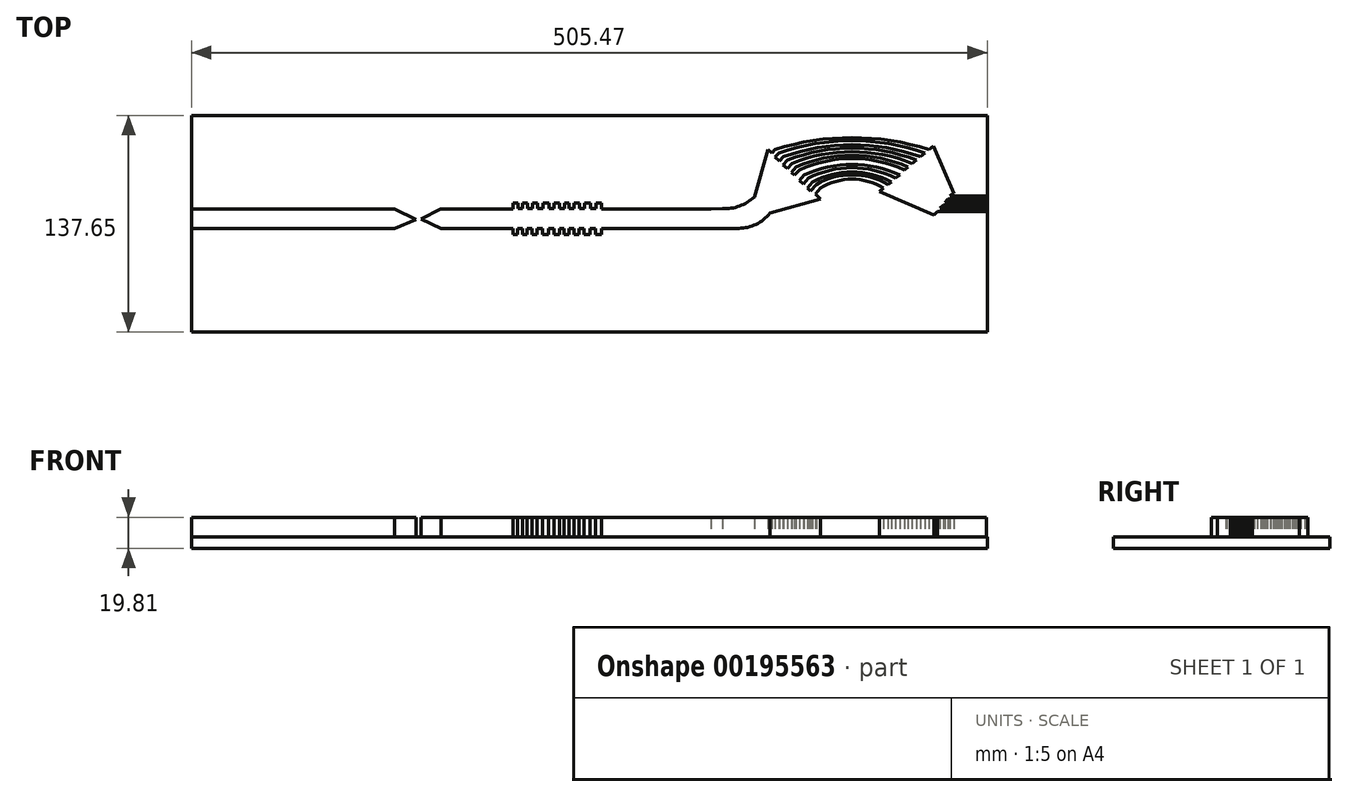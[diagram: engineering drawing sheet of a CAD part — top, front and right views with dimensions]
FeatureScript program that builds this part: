
annotation { "Feature Type Name" : "Feature", "Feature Type Description" : "" }
export const myFeature = defineFeature(function(context is Context, id is Id, definition is map)
    precondition{}
    {
        {
            var Q0;
            Q0=qCreatedBy(makeId("Top.planeOp"),FACE);
            var sketch = newSketch(context, id + "F0", { "sketchPlane" : qUnion([Q0])});
            skLineSegment(sketch, "E0.bottom", {"start": v(-20.52, -68.03) * mm, "end": v(484.95, -68.03) * mm});
            skLineSegment(sketch, "E0.top", {"start": v(-20.52, 69.62) * mm, "end": v(484.95, 69.62) * mm});
            skLineSegment(sketch, "E0.left", {"start": v(-20.52, -68.03) * mm, "end": v(-20.52, 69.62) * mm});
            skLineSegment(sketch, "E0.right", {"start": v(484.95, -68.03) * mm, "end": v(484.95, 69.62) * mm});
            skSolve(sketch);
        }
        {
            var Q0;
            Q0=qSketchRegion(id+"F0",true);
            extrude(context, id + "F1", {"entities" : qUnion([Q0]), "depth" : 7.37 * mm});
        }
        {
            var Q0;
            Q0=makeQuery(id+"F1.opExtrude","CAP_FACE",FACE,{"disambiguationData":[OSD([sQuery(id+"F0.wireOp",EDGE,"E0.bottom"),sQuery(id+"F0.wireOp",EDGE,"E0.top"),sQuery(id+"F0.wireOp",EDGE,"E0.left"),sQuery(id+"F0.wireOp",EDGE,"E0.right")])],"isStart":false});
            var sketch = newSketch(context, id + "F2", { "sketchPlane" : qUnion([Q0])});
            skLineSegment(sketch, "E1", {"start": v(183.86, 10.27) * mm, "end": v(183.86, 14.18) * mm});
            skLineSegment(sketch, "E2", {"start": v(183.86, 14.18) * mm, "end": v(186.92, 14.18) * mm});
            skLineSegment(sketch, "E3", {"start": v(186.92, 14.18) * mm, "end": v(186.92, 10.42) * mm});
            skLineSegment(sketch, "E4", {"start": v(186.92, 10.42) * mm, "end": v(189.9, 10.42) * mm});
            skLineSegment(sketch, "E5", {"start": v(189.9, 10.42) * mm, "end": v(189.9, 14.18) * mm});
            skLineSegment(sketch, "E6", {"start": v(189.9, 14.18) * mm, "end": v(192.9, 14.18) * mm});
            skLineSegment(sketch, "E7", {"start": v(192.9, 14.18) * mm, "end": v(192.9, 10.42) * mm});
            skLineSegment(sketch, "E8", {"start": v(192.9, 10.42) * mm, "end": v(196.13, 10.42) * mm});
            skLineSegment(sketch, "E9", {"start": v(196.13, 10.42) * mm, "end": v(196.13, 14.18) * mm});
            skLineSegment(sketch, "E10", {"start": v(196.13, 14.18) * mm, "end": v(199.35, 14.18) * mm});
            skLineSegment(sketch, "E11", {"start": v(199.35, 14.18) * mm, "end": v(199.35, 10.42) * mm});
            skLineSegment(sketch, "E12", {"start": v(199.35, 10.42) * mm, "end": v(202.73, 10.42) * mm});
            skLineSegment(sketch, "E13", {"start": v(202.73, 10.42) * mm, "end": v(202.73, 14.18) * mm});
            skLineSegment(sketch, "E14", {"start": v(202.73, 14.18) * mm, "end": v(206.5, 14.18) * mm});
            skLineSegment(sketch, "E15", {"start": v(206.5, 14.18) * mm, "end": v(206.5, 10.42) * mm});
            skLineSegment(sketch, "E16", {"start": v(206.5, 10.42) * mm, "end": v(209.87, 10.42) * mm});
            skLineSegment(sketch, "E17", {"start": v(209.87, 10.42) * mm, "end": v(209.87, 14.18) * mm});
            skLineSegment(sketch, "E18", {"start": v(209.87, 14.18) * mm, "end": v(213.4, 14.18) * mm});
            skLineSegment(sketch, "E19", {"start": v(213.4, 14.18) * mm, "end": v(213.4, 10.42) * mm});
            skLineSegment(sketch, "E20.MirrorCS", {"start": v(186.66, -5.84) * mm, "end": v(186.66, -2.08) * mm});
            skLineSegment(sketch, "E21.MirrorCS", {"start": v(199.1, -2.08) * mm, "end": v(202.48, -2.08) * mm});
            skLineSegment(sketch, "E22.MirrorCS", {"start": v(199.1, -5.84) * mm, "end": v(199.1, -2.08) * mm});
            skLineSegment(sketch, "E23.MirrorCS", {"start": v(189.66, -2.08) * mm, "end": v(189.66, -5.84) * mm});
            skLineSegment(sketch, "E24.MirrorCS", {"start": v(186.66, -2.08) * mm, "end": v(189.66, -2.08) * mm});
            skLineSegment(sketch, "E25.MirrorCS", {"start": v(202.48, -2.08) * mm, "end": v(202.48, -5.84) * mm});
            skLineSegment(sketch, "E26.MirrorCS", {"start": v(189.66, -5.84) * mm, "end": v(192.65, -5.84) * mm});
            skLineSegment(sketch, "E27.MirrorCS", {"start": v(202.48, -5.84) * mm, "end": v(206.24, -5.84) * mm});
            skLineSegment(sketch, "E28.MirrorCS", {"start": v(192.65, -5.84) * mm, "end": v(192.65, -2.08) * mm});
            skLineSegment(sketch, "E29.MirrorCS", {"start": v(192.65, -2.08) * mm, "end": v(195.87, -2.08) * mm});
            skLineSegment(sketch, "E30.MirrorCS", {"start": v(206.24, -5.84) * mm, "end": v(206.24, -2.08) * mm});
            skLineSegment(sketch, "E31.MirrorCS", {"start": v(195.87, -2.08) * mm, "end": v(195.87, -5.84) * mm});
            skLineSegment(sketch, "E32.MirrorCS", {"start": v(183.6, -5.84) * mm, "end": v(186.66, -5.84) * mm});
            skLineSegment(sketch, "E33.MirrorCS", {"start": v(206.24, -2.08) * mm, "end": v(209.62, -2.08) * mm});
            skLineSegment(sketch, "E34.MirrorCS", {"start": v(209.62, -2.08) * mm, "end": v(209.62, -5.84) * mm});
            skLineSegment(sketch, "E35.MirrorCS", {"start": v(195.87, -5.84) * mm, "end": v(199.1, -5.84) * mm});
            skLineSegment(sketch, "E36.MirrorCS", {"start": v(209.62, -5.84) * mm, "end": v(213.15, -5.84) * mm});
            skLineSegment(sketch, "E37.MirrorCS", {"start": v(183.61, -2.15) * mm, "end": v(183.6, -5.84) * mm});
            skLineSegment(sketch, "E38.MirrorCS", {"start": v(213.15, -5.84) * mm, "end": v(213.15, -2.08) * mm});
            skLineSegment(sketch, "E39", {"start": v(213.4, 10.42) * mm, "end": v(216.4, 10.42) * mm});
            skLineSegment(sketch, "E40", {"start": v(216.4, 10.42) * mm, "end": v(216.4, 14.18) * mm});
            skLineSegment(sketch, "E41", {"start": v(216.4, 14.18) * mm, "end": v(219.39, 14.18) * mm});
            skLineSegment(sketch, "E42", {"start": v(219.39, 14.18) * mm, "end": v(219.39, 10.42) * mm});
            skLineSegment(sketch, "E43", {"start": v(219.39, 10.42) * mm, "end": v(222.61, 10.42) * mm});
            skLineSegment(sketch, "E44", {"start": v(222.61, 10.42) * mm, "end": v(222.61, 14.18) * mm});
            skLineSegment(sketch, "E45", {"start": v(222.61, 14.18) * mm, "end": v(225.84, 14.18) * mm});
            skLineSegment(sketch, "E46", {"start": v(225.84, 14.18) * mm, "end": v(225.84, 10.42) * mm});
            skLineSegment(sketch, "E47", {"start": v(225.84, 10.42) * mm, "end": v(229.22, 10.42) * mm});
            skLineSegment(sketch, "E48", {"start": v(229.22, 10.42) * mm, "end": v(229.22, 14.18) * mm});
            skLineSegment(sketch, "E49", {"start": v(229.22, 14.18) * mm, "end": v(232.98, 14.18) * mm});
            skLineSegment(sketch, "E50", {"start": v(232.98, 14.18) * mm, "end": v(232.98, 10.42) * mm});
            skLineSegment(sketch, "E51", {"start": v(232.98, 10.42) * mm, "end": v(236.36, 10.42) * mm});
            skLineSegment(sketch, "E52", {"start": v(236.36, 10.42) * mm, "end": v(236.36, 14.18) * mm});
            skLineSegment(sketch, "E53", {"start": v(236.36, 14.18) * mm, "end": v(239.89, 14.18) * mm});
            skLineSegment(sketch, "E54", {"start": v(239.89, 14.18) * mm, "end": v(239.89, 10.33) * mm});
            skLineSegment(sketch, "E55.MirrorCS", {"start": v(225.58, -2.08) * mm, "end": v(228.96, -2.08) * mm});
            skLineSegment(sketch, "E56.MirrorCS", {"start": v(225.58, -5.84) * mm, "end": v(225.58, -2.08) * mm});
            skLineSegment(sketch, "E57.MirrorCS", {"start": v(216.14, -2.08) * mm, "end": v(216.14, -5.84) * mm});
            skLineSegment(sketch, "E58.MirrorCS", {"start": v(213.15, -2.08) * mm, "end": v(216.14, -2.08) * mm});
            skLineSegment(sketch, "E59.MirrorCS", {"start": v(228.96, -2.08) * mm, "end": v(228.96, -5.84) * mm});
            skLineSegment(sketch, "E60.MirrorCS", {"start": v(216.14, -5.84) * mm, "end": v(219.14, -5.84) * mm});
            skLineSegment(sketch, "E61.MirrorCS", {"start": v(228.96, -5.84) * mm, "end": v(232.72, -5.84) * mm});
            skLineSegment(sketch, "E62.MirrorCS", {"start": v(219.14, -5.84) * mm, "end": v(219.14, -2.08) * mm});
            skLineSegment(sketch, "E63.MirrorCS", {"start": v(219.14, -2.08) * mm, "end": v(222.36, -2.08) * mm});
            skLineSegment(sketch, "E64.MirrorCS", {"start": v(232.72, -5.84) * mm, "end": v(232.72, -2.08) * mm});
            skLineSegment(sketch, "E65.MirrorCS", {"start": v(222.36, -2.08) * mm, "end": v(222.36, -5.84) * mm});
            skLineSegment(sketch, "E66.MirrorCS", {"start": v(232.72, -2.08) * mm, "end": v(236.1, -2.08) * mm});
            skLineSegment(sketch, "E67.MirrorCS", {"start": v(236.1, -2.08) * mm, "end": v(236.1, -5.84) * mm});
            skLineSegment(sketch, "E68.MirrorCS", {"start": v(222.36, -5.84) * mm, "end": v(225.58, -5.84) * mm});
            skLineSegment(sketch, "E69.MirrorCS", {"start": v(236.1, -5.84) * mm, "end": v(239.89, -5.84) * mm});
            skLineSegment(sketch, "E70.MirrorCS", {"start": v(239.89, -5.84) * mm, "end": v(239.89, -2.04) * mm});
            skLineSegment(sketch, "E71", {"start": v(183.86, 10.27) * mm, "end": v(181.75, 10.28) * mm});
            skLineSegment(sketch, "E72", {"start": v(183.61, -2.15) * mm, "end": v(181.73, -2.15) * mm});
            skLineSegment(sketch, "E73", {"start": v(345.62, 48.01) * mm, "end": v(348.2, 45.76) * mm});
            skLineSegment(sketch, "E74", {"start": v(348.2, 45.76) * mm, "end": v(350.17, 48.01) * mm});
            skLineSegment(sketch, "E75", {"start": v(352.55, 45.93) * mm, "end": v(350.17, 43.2) * mm});
            skLineSegment(sketch, "E76", {"start": v(350.17, 43.2) * mm, "end": v(353.08, 40.66) * mm});
            skLineSegment(sketch, "E77", {"start": v(353.08, 40.66) * mm, "end": v(355.57, 43.5) * mm});
            skLineSegment(sketch, "E78", {"start": v(358.09, 41.3) * mm, "end": v(355.33, 38.15) * mm});
            skLineSegment(sketch, "E79", {"start": v(355.33, 38.15) * mm, "end": v(358.04, 35.78) * mm});
            skLineSegment(sketch, "E80", {"start": v(358.04, 35.78) * mm, "end": v(361.02, 39.19) * mm});
            skLineSegment(sketch, "E81", {"start": v(363.44, 36.92) * mm, "end": v(360.48, 33.54) * mm});
            skLineSegment(sketch, "E82", {"start": v(360.48, 33.54) * mm, "end": v(362.63, 31.66) * mm});
            skLineSegment(sketch, "E83", {"start": v(362.63, 31.66) * mm, "end": v(365.64, 35.1) * mm});
            skLineSegment(sketch, "E84", {"start": v(368.63, 31.74) * mm, "end": v(365.64, 28.32) * mm});
            skLineSegment(sketch, "E85", {"start": v(365.64, 28.32) * mm, "end": v(368.06, 26.2) * mm});
            skLineSegment(sketch, "E86", {"start": v(368.06, 26.2) * mm, "end": v(371.28, 29.87) * mm});
            skLineSegment(sketch, "E87", {"start": v(374.05, 27.44) * mm, "end": v(370.64, 23.53) * mm});
            skLineSegment(sketch, "E88", {"start": v(370.64, 23.53) * mm, "end": v(372.72, 21.7) * mm});
            skLineSegment(sketch, "E89", {"start": v(372.72, 21.7) * mm, "end": v(376.3, 25.8) * mm});
            skLineSegment(sketch, "E90", {"start": v(379.04, 23.42) * mm, "end": v(375.7, 19.6) * mm});
            skLineSegment(sketch, "E91", {"start": v(375.7, 19.6) * mm, "end": v(379.04, 16.68) * mm});
            skArc(sketch, "E92", {"start": v(379.04, 23.42) * mm, "mid": v(399, 29.22) * mm, "end": v(418.98, 23.42) * mm});
            skArc(sketch, "E93", {"start": v(376.3, 25.8) * mm, "mid": v(399, 31.93) * mm, "end": v(421.7, 25.8) * mm});
            skArc(sketch, "E94", {"start": v(374.05, 27.44) * mm, "mid": v(399, 33.78) * mm, "end": v(423.96, 27.44) * mm});
            skArc(sketch, "E95", {"start": v(371.28, 29.87) * mm, "mid": v(399, 36.4) * mm, "end": v(426.74, 29.87) * mm});
            skArc(sketch, "E96", {"start": v(368.63, 31.74) * mm, "mid": v(399, 38.53) * mm, "end": v(429.38, 31.74) * mm});
            skArc(sketch, "E97", {"start": v(365.64, 35.1) * mm, "mid": v(399, 42.27) * mm, "end": v(432.38, 35.1) * mm});
            skArc(sketch, "E98", {"start": v(363.44, 36.92) * mm, "mid": v(399, 44.28) * mm, "end": v(434.58, 36.92) * mm});
            skArc(sketch, "E99", {"start": v(361.02, 39.19) * mm, "mid": v(399, 46.64) * mm, "end": v(437, 39.19) * mm});
            skArc(sketch, "E100", {"start": v(358.09, 41.3) * mm, "mid": v(399, 48.93) * mm, "end": v(439.93, 41.3) * mm});
            skArc(sketch, "E101", {"start": v(355.57, 43.5) * mm, "mid": v(399, 51.1) * mm, "end": v(442.44, 43.5) * mm});
            skArc(sketch, "E102", {"start": v(352.55, 45.93) * mm, "mid": v(399, 53.68) * mm, "end": v(445.47, 45.93) * mm});
            skArc(sketch, "E103", {"start": v(350.17, 48.01) * mm, "mid": v(399, 55.56) * mm, "end": v(447.85, 48.01) * mm});
            skLineSegment(sketch, "E104", {"start": v(421.7, 25.8) * mm, "end": v(423.96, 27.44) * mm});
            skLineSegment(sketch, "E105", {"start": v(426.74, 29.87) * mm, "end": v(429.38, 31.74) * mm});
            skLineSegment(sketch, "E106", {"start": v(432.38, 35.1) * mm, "end": v(434.58, 36.92) * mm});
            skLineSegment(sketch, "E107", {"start": v(437, 39.19) * mm, "end": v(439.93, 41.3) * mm});
            skLineSegment(sketch, "E108", {"start": v(442.44, 43.5) * mm, "end": v(445.47, 45.93) * mm});
            skLineSegment(sketch, "E109", {"start": v(418.98, 23.42) * mm, "end": v(416.37, 21.29) * mm});
            skLineSegment(sketch, "E110", {"start": v(416.37, 21.29) * mm, "end": v(450.94, 6.45) * mm});
            skLineSegment(sketch, "E111", {"start": v(447.85, 48.01) * mm, "end": v(450.59, 50.33) * mm});
            skLineSegment(sketch, "E112", {"start": v(450.59, 50.33) * mm, "end": v(463.67, 20.17) * mm});
            skLineSegment(sketch, "E113", {"start": v(463.67, 20.17) * mm, "end": v(461.3, 18.35) * mm});
            skLineSegment(sketch, "E114", {"start": v(461.3, 18.35) * mm, "end": v(484.43, 18.35) * mm});
            skLineSegment(sketch, "E115", {"start": v(460.04, 16.54) * mm, "end": v(484.43, 16.54) * mm});
            skLineSegment(sketch, "E116", {"start": v(450.94, 6.45) * mm, "end": v(453.3, 8.59) * mm});
            skLineSegment(sketch, "E117", {"start": v(453.3, 8.59) * mm, "end": v(484.43, 8.59) * mm});
            skLineSegment(sketch, "E118", {"start": v(455, 10.82) * mm, "end": v(484.43, 10.82) * mm});
            skLineSegment(sketch, "E119", {"start": v(457.05, 12.63) * mm, "end": v(484.43, 12.63) * mm});
            skLineSegment(sketch, "E120", {"start": v(457.95, 14.45) * mm, "end": v(484.43, 14.45) * mm});
            skLineSegment(sketch, "E121", {"start": v(457.95, 14.45) * mm, "end": v(460.04, 16.54) * mm});
            skLineSegment(sketch, "E122", {"start": v(457.05, 12.63) * mm, "end": v(455, 10.82) * mm});
            skLineSegment(sketch, "E123", {"start": v(484.43, 18.35) * mm, "end": v(484.43, 16.54) * mm});
            skLineSegment(sketch, "E124", {"start": v(484.43, 14.45) * mm, "end": v(484.43, 12.63) * mm});
            skLineSegment(sketch, "E125", {"start": v(484.43, 10.82) * mm, "end": v(484.43, 8.59) * mm});
            skLineSegment(sketch, "E126", {"start": v(122.05, 3.65) * mm, "end": v(108.54, 10.35) * mm});
            skLineSegment(sketch, "E127", {"start": v(108.54, 10.35) * mm, "end": v(-20.32, 10.35) * mm});
            skLineSegment(sketch, "E128", {"start": v(122.05, 3.65) * mm, "end": v(108.45, -2.18) * mm});
            skLineSegment(sketch, "E129", {"start": v(108.45, -2.18) * mm, "end": v(-20.52, -2.18) * mm});
            skLineSegment(sketch, "E130", {"start": v(-20.52, -2.18) * mm, "end": v(-20.32, 10.35) * mm});
            skLineSegment(sketch, "E131", {"start": v(125.38, 4.02) * mm, "end": v(137.78, 10.35) * mm});
            skLineSegment(sketch, "E132", {"start": v(137.78, 10.35) * mm, "end": v(174.26, 10.35) * mm});
            skLineSegment(sketch, "E133", {"start": v(125.38, 4.02) * mm, "end": v(138.02, -2.18) * mm});
            skLineSegment(sketch, "E134", {"start": v(138.02, -2.18) * mm, "end": v(174.02, -2.18) * mm});
            skLineSegment(sketch, "E135", {"start": v(181.75, 10.28) * mm, "end": v(174.26, 10.35) * mm});
            skLineSegment(sketch, "E136", {"start": v(181.73, -2.15) * mm, "end": v(174.02, -2.18) * mm});
            skLineSegment(sketch, "E137", {"start": v(239.89, 10.33) * mm, "end": v(309.51, 10.33) * mm});
            skLineSegment(sketch, "E138", {"start": v(239.89, -2.04) * mm, "end": v(308.71, -2.04) * mm});
            skArc(sketch, "E139", {"start": v(316.74, 10.47) * mm, "mid": v(327.63, 12.1) * mm, "end": v(336.95, 17.97) * mm});
            skLineSegment(sketch, "E140", {"start": v(336.95, 17.97) * mm, "end": v(345.62, 48.01) * mm});
            skLineSegment(sketch, "E141", {"start": v(316.74, 10.47) * mm, "end": v(309.51, 10.33) * mm});
            skLineSegment(sketch, "E142", {"start": v(308.71, -2.04) * mm, "end": v(327.09, -2.04) * mm});
            skArc(sketch, "E143", {"start": v(327.09, -2.04) * mm, "mid": v(338.07, 0.5) * mm, "end": v(346.85, 7.56) * mm});
            skLineSegment(sketch, "E144", {"start": v(346.85, 7.56) * mm, "end": v(379.04, 16.68) * mm});
            skSolve(sketch);
        }
        {
            var Q0;
            Q0=qSketchRegion(id+"F2",true);
            var Q1;
            Q1=makeQuery(id+"F2.imprint","IMPRINT",FACE,{"disambiguationData":[TD([[makeQuery(id+"F2.imprint","IMPRINT",EDGE,{"derivedFrom":sQuery(id+"F2.wireOp",EDGE,"0cfBDwDP-kQ9P-NFsK-J92y-6gZ9nuPkPhFx.bottom")}),-1.0]])]});
            var Q2;
            Q2=makeQuery(id+"F2.imprint","IMPRINT",FACE,{"disambiguationData":[TD([[makeQuery(id+"F2.imprint","IMPRINT",EDGE,{"derivedFrom":sQuery(id+"F2.wireOp",EDGE,"a9ZTMBmW-VK13-Soqm-w6V6-YXW0XHa0mt64.bottom")}),-1.0]])]});
            var Q3;
            Q3=makeQuery(id+"F2.imprint","IMPRINT",FACE,{"disambiguationData":[TD([[makeQuery(id+"F2.imprint","IMPRINT",EDGE,{"derivedFrom":sQuery(id+"F2.wireOp",EDGE,"acd87d69-ad82-4e63-a43d-dcfdde5fbf36.bottom")}),-1.0]])]});
            extrude(context, id + "F3", {"entities" : qUnion([Q0, Q1, Q2, Q3]), "operationType" : NewBodyOperationType.ADD, "depth" : 12.45 * mm});
        }
        {
            var Q0;
            Q0=makeQuery(id+"F1.opExtrude","SWEPT_FACE",FACE,{"disambiguationData":[OSD([sQuery(id+"F0.wireOp",EDGE,"E0.right")])]});
            cPlane(context, id + "F4", {"entities" : qUnion([Q0]), "cplaneType" : CPlaneType.OFFSET, "offset" : 25.4 * mm, "width" : 152.4 * mm, "height" : 152.4 * mm});
        }
    });
